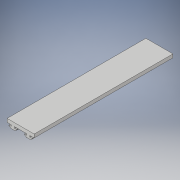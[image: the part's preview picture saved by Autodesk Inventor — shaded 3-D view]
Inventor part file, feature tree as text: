
AUTODESK INVENTOR PART (.ipt)
format: ipt  version: 2017 (Build 210142000, 142)  size: 128,512 bytes
history: native  units: in
note: dims shown in document units (in); Inventor stores cm internally (conversion verified against a paired STEP export)
features: extrude x1, mirror x1, sketch x1
ambient origin geometry x8: Origin, YZ Plane, XZ Plane, XY Plane, X Axis, Y Axis, Z Axis, Center Point
bodies: Solid1 (feature_tree)
feature tree (3):
  extrude  "Extrusion1"  Depth=0.0787in
  mirror  "Mirror1"
  sketch  "Sketch1"  dims[d0=0.6693in d2=0.1969in d3=0.0787in d4=0.1874in d6=0.4524in d7=0.1085in d8=0.225in d9=0.2221in d10=0.2409in d11=0.03in d12=0.03in d13=8.0in d14=0.0in d50=0.9949in d51=0.1137in d53=0.4337in]
